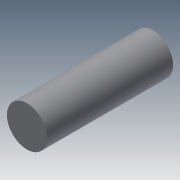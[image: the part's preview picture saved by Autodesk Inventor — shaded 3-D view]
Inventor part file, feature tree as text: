
AUTODESK INVENTOR PART (.ipt)
format: ipt  version: 2013 (Build 170138000, 138)  size: 69,632 bytes
history: native  units: mm
features: extrude x1, sketch x1
ambient origin geometry x8: Origin, YZ Plane, XZ Plane, XY Plane, X Axis, Y Axis, Z Axis, Center Point
bodies: Solid1 (feature_tree)
feature tree (2):
  extrude  "Extrusion1"  Depth=22.0mm TaperAngle=0.0deg
  sketch  "Sketch1"  dims[d0=7.0mm d1=22.0mm d2=0.0mm]
